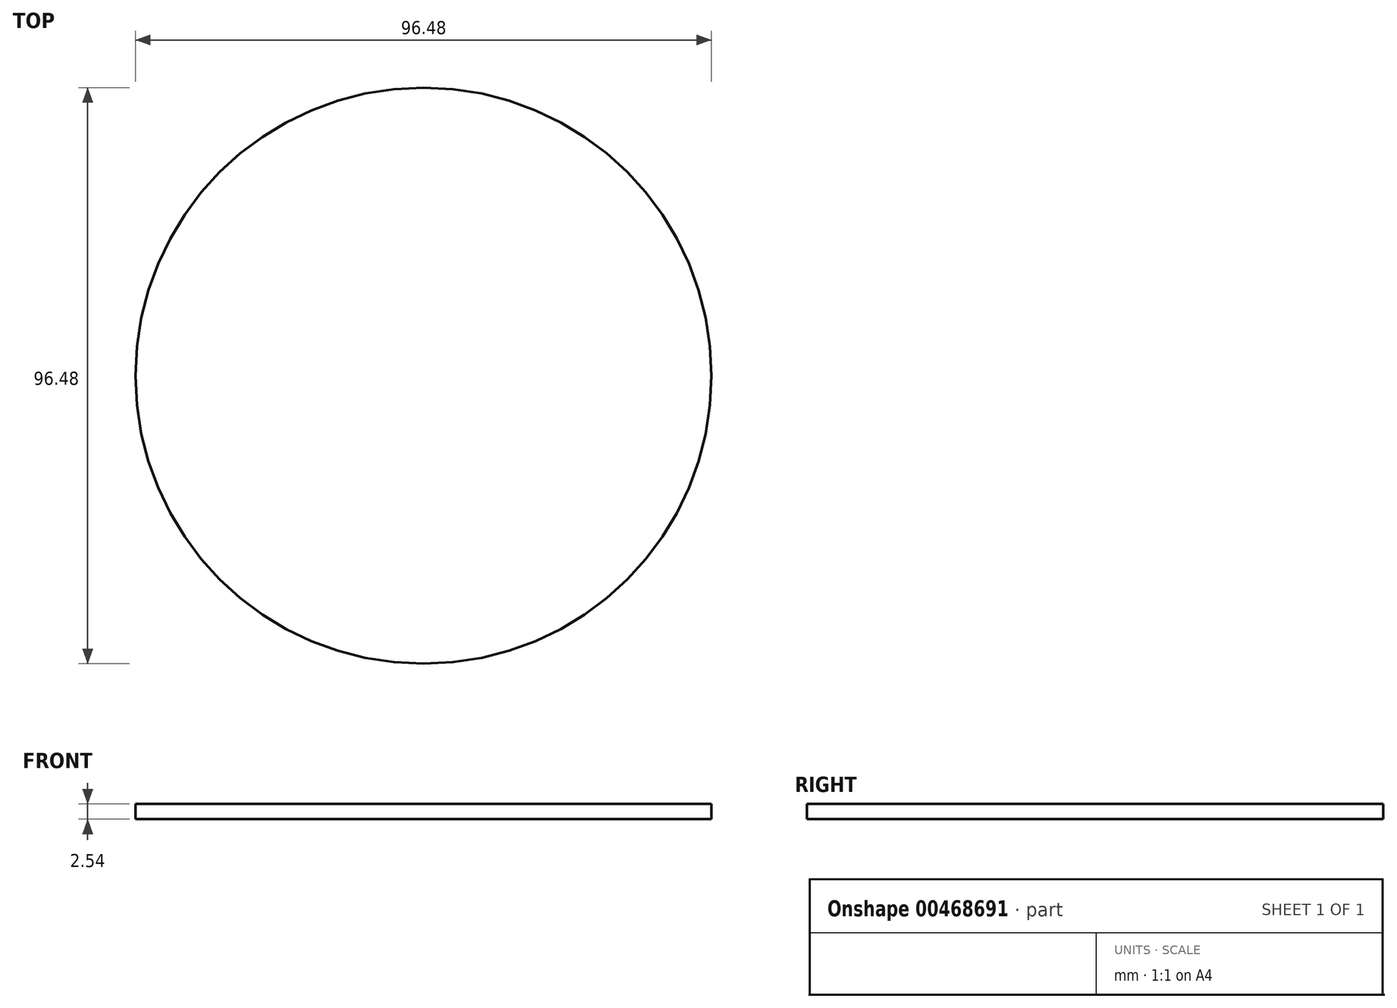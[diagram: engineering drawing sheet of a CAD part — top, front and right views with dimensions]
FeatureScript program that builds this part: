
annotation { "Feature Type Name" : "Feature", "Feature Type Description" : "" }
export const myFeature = defineFeature(function(context is Context, id is Id, definition is map)
    precondition{}
    {
        {
            var Q0;
            Q0=qCreatedBy(makeId("Top.planeOp"),FACE);
            var sketch = newSketch(context, id + "F0", { "sketchPlane" : qUnion([Q0])});
            skCircle(sketch, "E0", {"center": v(0, 0) * mm, "radius": 27.4 * mm});
            skCircle(sketch, "E1", {"center": v(0, 0) * mm, "radius": 17.3 * mm});
            skSolve(sketch);
        }
        {
            var Q0;
            Q0=sQuery(id+"F0.wireOp",EDGE,"E0");
            var Q1;
            Q1=sQuery(id+"F0.wireOp",EDGE,"E1");
            extrude(context, id + "F1", {"bodyType" : ToolBodyType.SURFACE, "surfaceEntities" : qUnion([Q0, Q1]), "depth" : 26.42 * mm});
        }
        {
            var Q0;
            Q0=qCreatedBy(makeId("Top.planeOp"),FACE);
            var sketch = newSketch(context, id + "F2", { "sketchPlane" : qUnion([Q0])});
            skCircle(sketch, "E2", {"center": v(-10, 16.3) * mm, "radius": 48.24 * mm});
            skSolve(sketch);
        }
        {
            var Q0;
            Q0=makeQuery(id+"F2.imprint","IMPRINT",FACE,{"disambiguationData":[TD([[makeQuery(id+"F2.imprint","IMPRINT",EDGE,{"derivedFrom":sQuery(id+"F2.wireOp",EDGE,"E2")}),1.0]])]});
            extrude(context, id + "F3", {"entities" : qUnion([Q0]), "depth" : 2.54 * mm});
        }
    });
